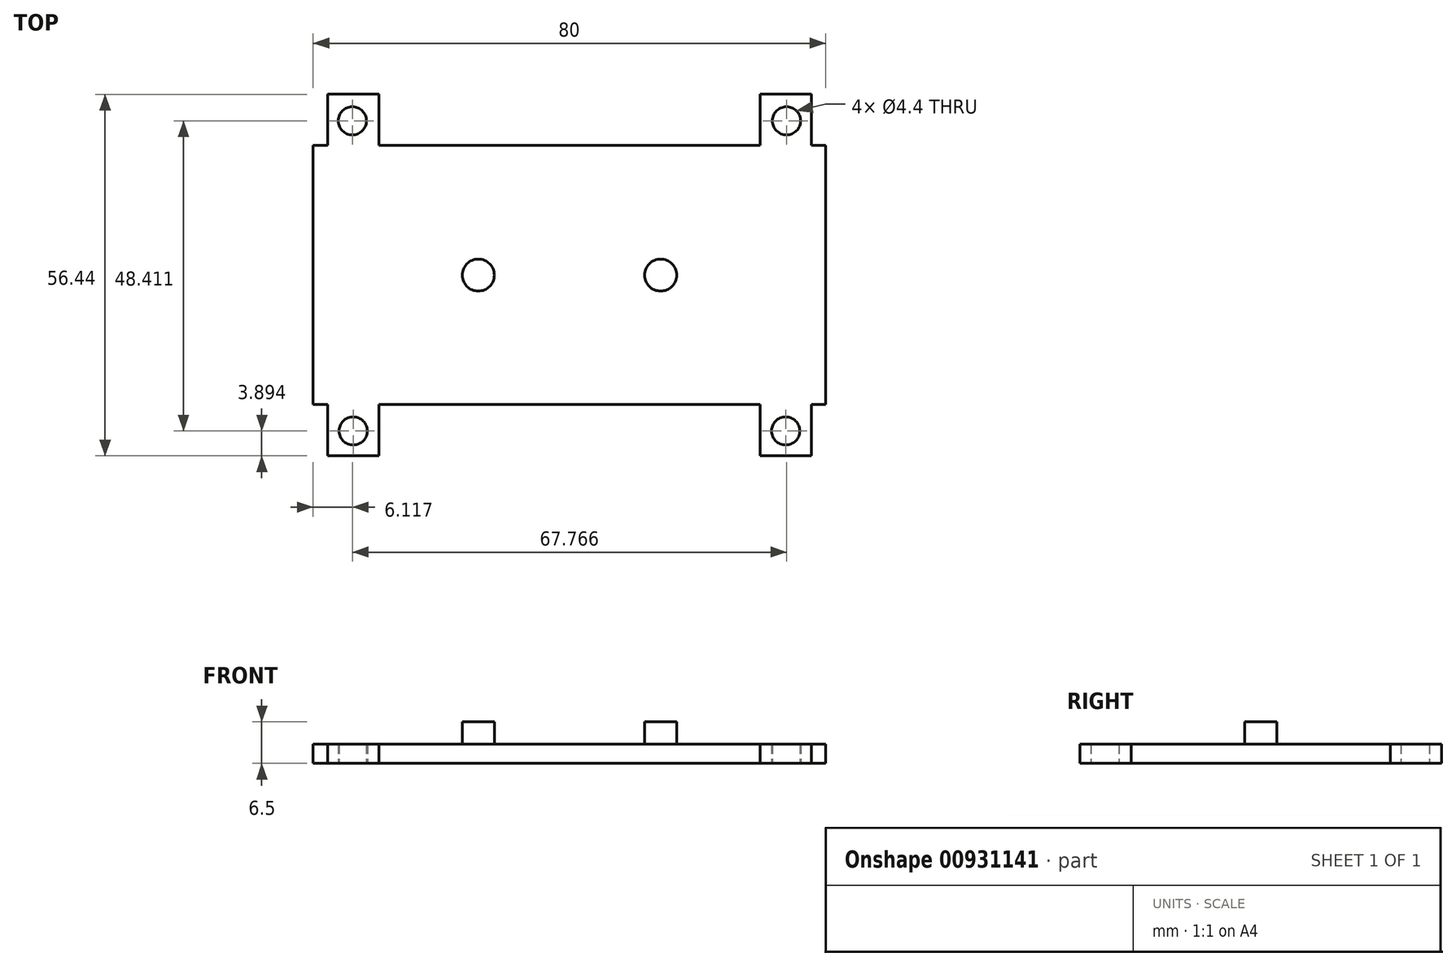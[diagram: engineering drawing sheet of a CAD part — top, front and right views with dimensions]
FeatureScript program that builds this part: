
annotation { "Feature Type Name" : "Feature", "Feature Type Description" : "" }
export const myFeature = defineFeature(function(context is Context, id is Id, definition is map)
    precondition{}
    {
        {
            var Q0;
            Q0=qCreatedBy(makeId("Top.planeOp"),FACE);
            var sketch = newSketch(context, id + "F0", { "sketchPlane" : qUnion([Q0])});
            skLineSegment(sketch, "E0.bottom", {"start": v(-40, 20.22) * mm, "end": v(40, 20.22) * mm});
            skLineSegment(sketch, "E0.top", {"start": v(-40, -20.22) * mm, "end": v(40, -20.22) * mm});
            skLineSegment(sketch, "E0.left", {"start": v(-40, 20.22) * mm, "end": v(-40, -20.22) * mm});
            skLineSegment(sketch, "E0.right", {"start": v(40, 20.22) * mm, "end": v(40, -20.22) * mm});
            skPoint(sketch, "E0.middle", {"position": v(0, 0) * mm});
            skLineSegment(sketch, "E1.bottom", {"start": v(-37.77, 20.22) * mm, "end": v(-29.77, 20.22) * mm});
            skLineSegment(sketch, "E1.top", {"start": v(-37.77, 28.22) * mm, "end": v(-29.77, 28.22) * mm});
            skLineSegment(sketch, "E1.left", {"start": v(-37.77, 20.22) * mm, "end": v(-37.77, 28.22) * mm});
            skLineSegment(sketch, "E1.right", {"start": v(-29.77, 20.22) * mm, "end": v(-29.77, 28.22) * mm});
            skLineSegment(sketch, "E2.bottom", {"start": v(36.19, 20.22) * mm, "end": v(28.19, 20.22) * mm});
            skLineSegment(sketch, "E3.bottom", {"start": v(-37.77, -20.22) * mm, "end": v(-29.77, -20.22) * mm});
            skLineSegment(sketch, "E3.top", {"start": v(-37.77, -28.22) * mm, "end": v(-29.77, -28.22) * mm});
            skLineSegment(sketch, "E3.left", {"start": v(-37.77, -20.22) * mm, "end": v(-37.77, -28.22) * mm});
            skLineSegment(sketch, "E3.right", {"start": v(-29.77, -20.22) * mm, "end": v(-29.77, -28.22) * mm});
            skLineSegment(sketch, "E4.MirrorCS", {"start": v(37.77, 20.22) * mm, "end": v(37.77, 28.22) * mm});
            skLineSegment(sketch, "E5.MirrorCS", {"start": v(37.77, 28.22) * mm, "end": v(29.77, 28.22) * mm});
            skLineSegment(sketch, "E6.MirrorCS", {"start": v(29.77, 20.22) * mm, "end": v(29.77, 28.22) * mm});
            skLineSegment(sketch, "E7.MirrorCS", {"start": v(29.77, -20.22) * mm, "end": v(29.77, -28.22) * mm});
            skLineSegment(sketch, "E8.MirrorCS", {"start": v(37.77, -28.22) * mm, "end": v(29.77, -28.22) * mm});
            skLineSegment(sketch, "E9.MirrorCS", {"start": v(37.77, -20.22) * mm, "end": v(37.77, -28.22) * mm});
            skSolve(sketch);
        }
        {
            var Q0;
            Q0 = qSketchRegion(id + "F0", true);
            extrude(context, id + "F1", {"entities" : qUnion([Q0]), "depth" : 3 * mm, "offsetDistance" : 25 * mm});
        }
        {
            var Q0;
            Q0=qCreatedBy(makeId("Top.planeOp"),FACE);
            var sketch = newSketch(context, id + "F2", { "sketchPlane" : qUnion([Q0])});
            skCircle(sketch, "E10", {"center": v(-33.88, 24.09) * mm, "radius": 2.2 * mm});
            skCircle(sketch, "E11", {"center": v(-33.75, -24.33) * mm, "radius": 2.2 * mm});
            skCircle(sketch, "E12.MirrorC", {"center": v(33.88, 24.09) * mm, "radius": 2.2 * mm});
            skCircle(sketch, "E13.MirrorC", {"center": v(33.75, -24.33) * mm, "radius": 2.2 * mm});
            skSolve(sketch);
        }
        {
            var Q0;
            Q0 = qSketchRegion(id + "F2", true);
            extrude(context, id + "F3", {"entities" : qUnion([Q0]), "operationType" : NewBodyOperationType.REMOVE, "depth" : 5 * mm, "offsetDistance" : 25 * mm});
        }
        {
            var Q0;
            Q0=qCreatedBy(makeId("Top.planeOp"),FACE);
            var sketch = newSketch(context, id + "F4", { "sketchPlane" : qUnion([Q0])});
            skCircle(sketch, "E14", {"center": v(-14.23, 0) * mm, "radius": 2.5 * mm});
            skCircle(sketch, "E15.MirrorC", {"center": v(14.23, 0) * mm, "radius": 2.5 * mm});
            skSolve(sketch);
        }
        {
            var Q0;
            Q0 = qSketchRegion(id + "F4", true);
            extrude(context, id + "F5", {"entities" : qUnion([Q0]), "operationType" : NewBodyOperationType.ADD, "depth" : 6.5 * mm, "offsetDistance" : 25 * mm});
        }
    });
